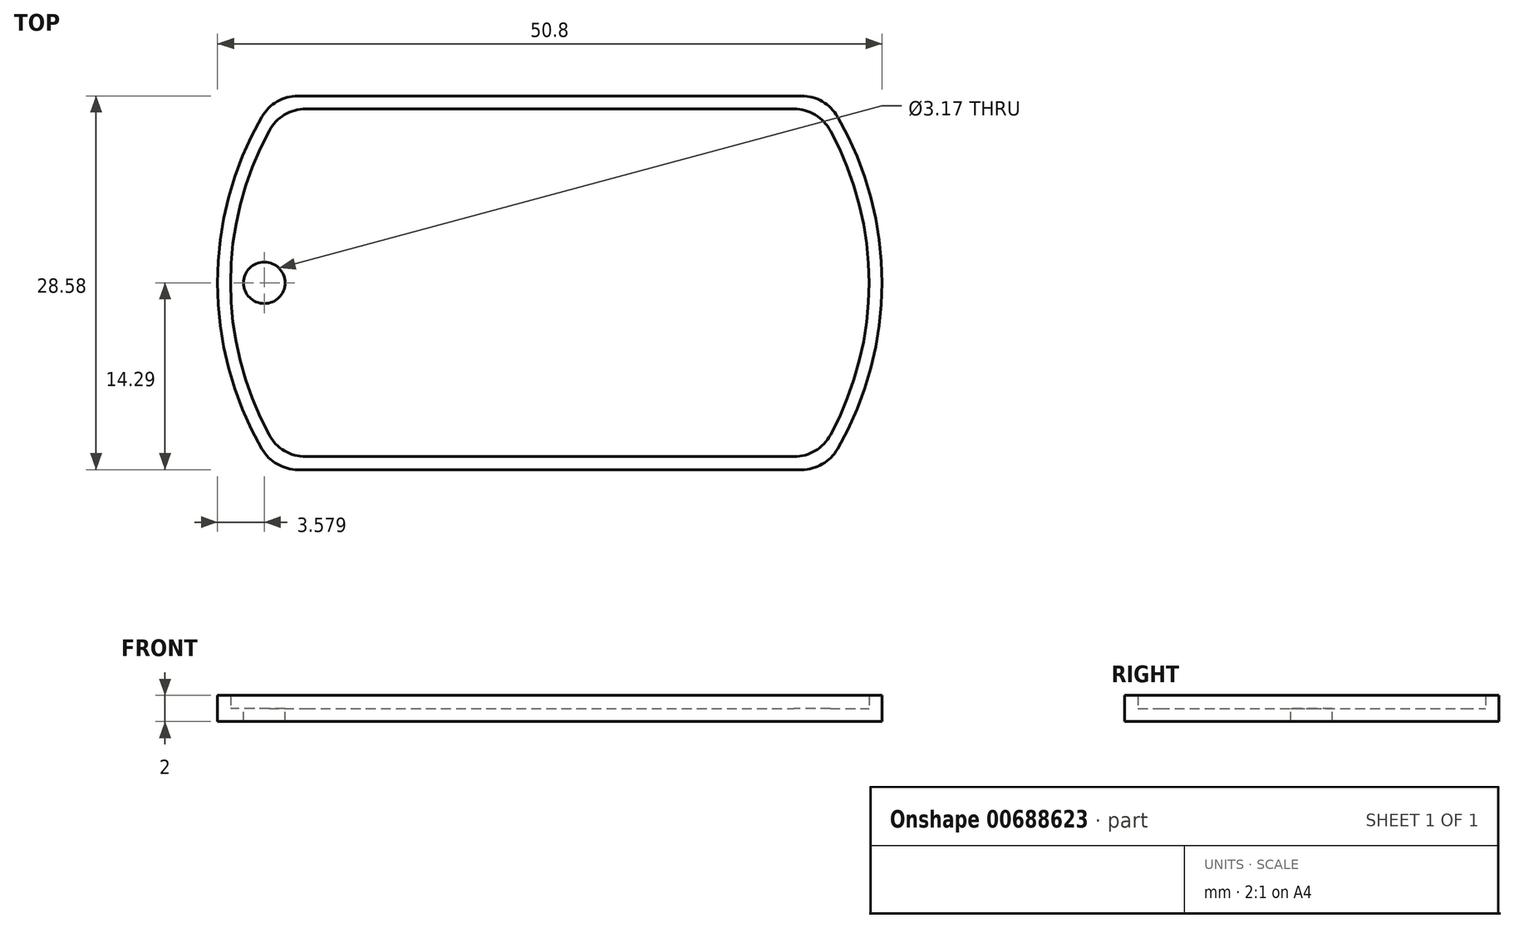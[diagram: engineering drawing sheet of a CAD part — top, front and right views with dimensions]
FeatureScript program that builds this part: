
annotation { "Feature Type Name" : "Feature", "Feature Type Description" : "" }
export const myFeature = defineFeature(function(context is Context, id is Id, definition is map)
    precondition{}
    {
        {
            var Q0;
            Q0=qCreatedBy(makeId("Top.planeOp"),FACE);
            var sketch = newSketch(context, id + "F0", { "sketchPlane" : qUnion([Q0])});
            skArc(sketch, "E0", {"start": v(-22, 12.7) * mm, "mid": v(-25.4, 0) * mm, "end": v(-22, -12.7) * mm});
            skLineSegment(sketch, "E1.top", {"start": v(-19.25, -14.29) * mm, "end": v(19.25, -14.29) * mm});
            skArc(sketch, "E2.trimOffspring", {"start": v(22, -12.7) * mm, "mid": v(25.4, 0) * mm, "end": v(22, 12.7) * mm});
            skLineSegment(sketch, "E3", {"start": v(-19.25, 14.29) * mm, "end": v(19.25, 14.29) * mm});
            skPoint(sketch, "E4.visualSharp", {"position": v(-21, 14.29) * mm});
            skArc(sketch, "E4.filletArc", {"start": v(-19.25, 14.29) * mm, "mid": v(-20.83, 13.86) * mm, "end": v(-22, 12.7) * mm});
            skPoint(sketch, "E5.visualSharp", {"position": v(21, 14.29) * mm});
            skArc(sketch, "E5.filletArc", {"start": v(22, 12.7) * mm, "mid": v(20.83, 13.86) * mm, "end": v(19.25, 14.29) * mm});
            skPoint(sketch, "E6.visualSharp", {"position": v(21, -14.29) * mm});
            skArc(sketch, "E6.filletArc", {"start": v(19.25, -14.29) * mm, "mid": v(20.83, -13.86) * mm, "end": v(22, -12.7) * mm});
            skPoint(sketch, "E7.visualSharp", {"position": v(-21, -14.29) * mm});
            skArc(sketch, "E7.filletArc", {"start": v(-22, -12.7) * mm, "mid": v(-20.83, -13.86) * mm, "end": v(-19.25, -14.29) * mm});
            skSolve(sketch);
        }
        {
            var Q0;
            Q0=makeQuery(id+"F0.imprint","IMPRINT",FACE,{"disambiguationData":[TD([[makeQuery(id+"F0.imprint","IMPRINT",EDGE,{"derivedFrom":sQuery(id+"F0.wireOp",EDGE,"E0")}),1.0]])]});
            extrude(context, id + "F1", {"entities" : qUnion([Q0]), "depth" : 1 * mm, "offsetDistance" : 25.4 * mm});
        }
        {
            var Q0;
            Q0=makeQuery(id+"F1.opExtrude","CAP_FACE",FACE,{"disambiguationData":[OSD([sQuery(id+"F0.wireOp",EDGE,"E0"),sQuery(id+"F0.wireOp",EDGE,"E1.top"),sQuery(id+"F0.wireOp",EDGE,"E2.trimOffspring"),sQuery(id+"F0.wireOp",EDGE,"E3"),sQuery(id+"F0.wireOp",EDGE,"E4.filletArc"),sQuery(id+"F0.wireOp",EDGE,"E5.filletArc"),sQuery(id+"F0.wireOp",EDGE,"E6.filletArc"),sQuery(id+"F0.wireOp",EDGE,"E7.filletArc")])],"isStart":false});
            var sketch = newSketch(context, id + "F2", { "sketchPlane" : qUnion([Q0])});
            skLineSegment(sketch, "E8.0", {"start": v(-18.66, 13.29) * mm, "end": v(18.66, 13.29) * mm});
            skArc(sketch, "E8.1", {"start": v(-21.45, 11.63) * mm, "mid": v(-24.4, 0) * mm, "end": v(-21.45, -11.63) * mm});
            skLineSegment(sketch, "E8.2", {"start": v(-18.66, -13.29) * mm, "end": v(18.66, -13.29) * mm});
            skArc(sketch, "E8.3", {"start": v(21.45, -11.63) * mm, "mid": v(24.4, 0) * mm, "end": v(21.45, 11.63) * mm});
            skPoint(sketch, "E9.visualSharp", {"position": v(-20.46, 13.29) * mm});
            skArc(sketch, "E9.filletArc", {"start": v(-18.66, 13.29) * mm, "mid": v(-20.29, 12.84) * mm, "end": v(-21.45, 11.63) * mm});
            skPoint(sketch, "E10.visualSharp", {"position": v(20.46, 13.29) * mm});
            skArc(sketch, "E10.filletArc", {"start": v(21.45, 11.63) * mm, "mid": v(20.29, 12.84) * mm, "end": v(18.66, 13.29) * mm});
            skPoint(sketch, "E11.visualSharp", {"position": v(20.46, -13.29) * mm});
            skArc(sketch, "E11.filletArc", {"start": v(18.66, -13.29) * mm, "mid": v(20.29, -12.84) * mm, "end": v(21.45, -11.63) * mm});
            skPoint(sketch, "E12.visualSharp", {"position": v(-20.46, -13.29) * mm});
            skArc(sketch, "E12.filletArc", {"start": v(-21.45, -11.63) * mm, "mid": v(-20.29, -12.84) * mm, "end": v(-18.66, -13.29) * mm});
            skLineSegment(sketch, "E13.0", {"start": v(-19.25, 14.29) * mm, "end": v(19.25, 14.29) * mm});
            skArc(sketch, "E13.1", {"start": v(-22, 12.7) * mm, "mid": v(-25.4, 0) * mm, "end": v(-22, -12.7) * mm});
            skLineSegment(sketch, "E13.2", {"start": v(-19.25, -14.29) * mm, "end": v(19.25, -14.29) * mm});
            skArc(sketch, "E13.3", {"start": v(22, -12.7) * mm, "mid": v(25.4, 0) * mm, "end": v(22, 12.7) * mm});
            skPoint(sketch, "E14.visualSharp", {"position": v(-21, -14.29) * mm});
            skArc(sketch, "E14.filletArc", {"start": v(-22, -12.7) * mm, "mid": v(-20.83, -13.86) * mm, "end": v(-19.25, -14.29) * mm});
            skPoint(sketch, "E15.visualSharp", {"position": v(21, -14.29) * mm});
            skArc(sketch, "E15.filletArc", {"start": v(19.25, -14.29) * mm, "mid": v(20.83, -13.86) * mm, "end": v(22, -12.7) * mm});
            skPoint(sketch, "E16.visualSharp", {"position": v(21, 14.29) * mm});
            skArc(sketch, "E16.filletArc", {"start": v(22, 12.7) * mm, "mid": v(20.83, 13.86) * mm, "end": v(19.25, 14.29) * mm});
            skPoint(sketch, "E17.visualSharp", {"position": v(-21, 14.29) * mm});
            skArc(sketch, "E17.filletArc", {"start": v(-19.25, 14.29) * mm, "mid": v(-20.83, 13.86) * mm, "end": v(-22, 12.7) * mm});
            skSolve(sketch);
        }
        {
            var Q0;
            Q0=makeQuery(id+"F2.imprint","IMPRINT",FACE,{"disambiguationData":[TD([[makeQuery(id+"F2.imprint","IMPRINT",EDGE,{"derivedFrom":sQuery(id+"F2.wireOp",EDGE,"E8.0")}),1.0]])]});
            extrude(context, id + "F3", {"entities" : qUnion([Q0]), "operationType" : NewBodyOperationType.ADD, "depth" : 1 * mm, "offsetDistance" : 25.4 * mm});
        }
        {
            var Q0;
            Q0=makeQuery(id+"F1.opExtrude","CAP_FACE",FACE,{"disambiguationData":[OSD([sQuery(id+"F0.wireOp",EDGE,"E0"),sQuery(id+"F0.wireOp",EDGE,"E1.top"),sQuery(id+"F0.wireOp",EDGE,"E2.trimOffspring"),sQuery(id+"F0.wireOp",EDGE,"E3"),sQuery(id+"F0.wireOp",EDGE,"E4.filletArc"),sQuery(id+"F0.wireOp",EDGE,"E5.filletArc"),sQuery(id+"F0.wireOp",EDGE,"E6.filletArc"),sQuery(id+"F0.wireOp",EDGE,"E7.filletArc")])],"isStart":false});
            var sketch = newSketch(context, id + "F4", { "sketchPlane" : qUnion([Q0])});
            skCircle(sketch, "E18", {"center": v(-21.82, 0) * mm, "radius": 1.59 * mm});
            skSolve(sketch);
        }
        {
            var Q0;
            Q0=makeQuery(id+"F4.imprint","IMPRINT",FACE,{"disambiguationData":[TD([[makeQuery(id+"F4.imprint","IMPRINT",EDGE,{"derivedFrom":sQuery(id+"F4.wireOp",EDGE,"E18")}),1.0]])]});
            extrude(context, id + "F5", {"entities" : qUnion([Q0]), "operationType" : NewBodyOperationType.REMOVE, "oppositeDirection" : true, "depth" : 1 * mm, "offsetDistance" : 25.4 * mm});
        }
        {
            var Q0;
            Q0=makeQuery(id+"F1.opExtrude","CAP_FACE",FACE,{"disambiguationData":[OSD([sQuery(id+"F0.wireOp",EDGE,"E0"),sQuery(id+"F0.wireOp",EDGE,"E1.top"),sQuery(id+"F0.wireOp",EDGE,"E2.trimOffspring"),sQuery(id+"F0.wireOp",EDGE,"E3"),sQuery(id+"F0.wireOp",EDGE,"E4.filletArc"),sQuery(id+"F0.wireOp",EDGE,"E5.filletArc"),sQuery(id+"F0.wireOp",EDGE,"E6.filletArc"),sQuery(id+"F0.wireOp",EDGE,"E7.filletArc")])],"isStart":false});
            var sketch = newSketch(context, id + "F6", { "sketchPlane" : qUnion([Q0])});
            skText(sketch, "E19", { "text": "Mr.TwoTimezz", "fontName": "OpenSans-Bold.ttf"});
            skText(sketch, "E20", { "text": "Rico", "fontName": "OpenSans-Regular.ttf"});
            const initialGuessF6  = {"E19": [-0.01973, 0, 1, 0, 0.00394], "E20": [-0.00768, -0.00914, 1, 0, 0.00595]};
            skSetInitialGuess(sketch, initialGuessF6);
            skSolve(sketch);
        }
        {
            var Q0;
            Q0 = qConstructionFilter(qBodyType(qCreatedBy(id + "F6" ,EDGE), BodyType.WIRE), ConstructionObject.NO);
            extrude(context, id + "F7", {"bodyType" : ToolBodyType.SURFACE, "surfaceEntities" : qUnion([Q0]), "depth" : 1 * mm, "offsetDistance" : 25.4 * mm});
        }
    });
